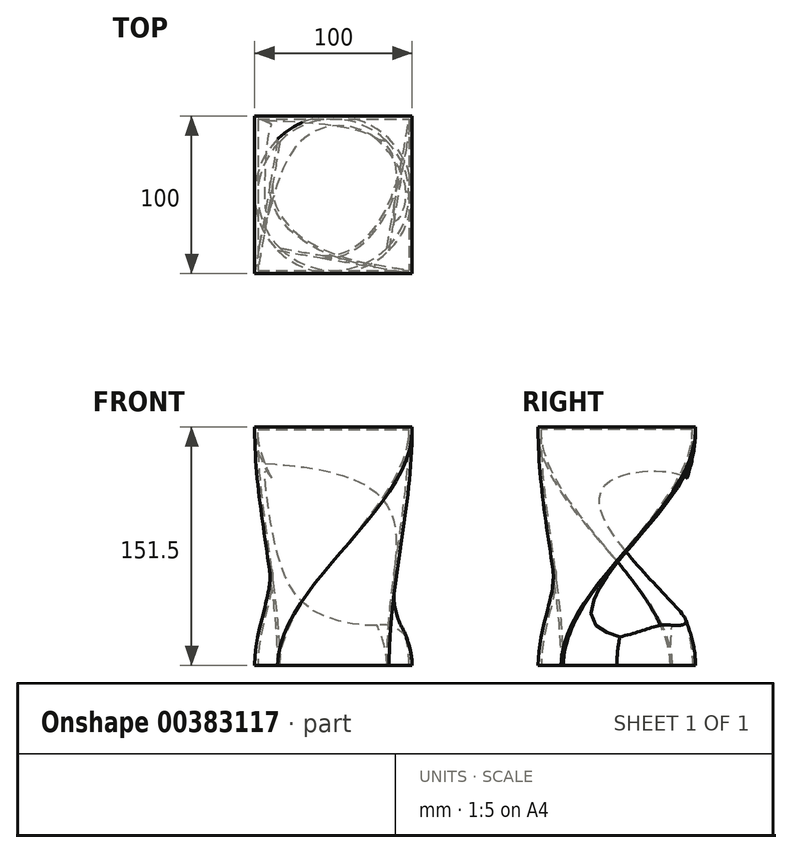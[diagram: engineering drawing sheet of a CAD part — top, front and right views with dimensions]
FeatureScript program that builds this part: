
annotation { "Feature Type Name" : "Feature", "Feature Type Description" : "" }
export const myFeature = defineFeature(function(context is Context, id is Id, definition is map)
    precondition{}
    {
        {
            var Q0;
            Q0=qCreatedBy(makeId("Top.planeOp"),FACE);
            var sketch = newSketch(context, id + "F0", { "sketchPlane" : qUnion([Q0])});
            skArc(sketch, "E0", {"start": v(-35.36, 35.36) * mm, "mid": v(-50, 0) * mm, "end": v(-35.36, -35.36) * mm});
            skArc(sketch, "E1", {"start": v(50, 0) * mm, "mid": v(19.13, 46.2) * mm, "end": v(-35.36, 35.36) * mm});
            skArc(sketch, "E2", {"start": v(-35.36, -35.36) * mm, "mid": v(35.36, -35.36) * mm, "end": v(35.36, 35.36) * mm});
            skArc(sketch, "E3", {"start": v(-35.36, -35.36) * mm, "mid": v(0, -50) * mm, "end": v(35.36, -35.36) * mm});
            skLineSegment(sketch, "E4", {"start": v(0, 57.4) * mm, "end": v(0, -65.17) * mm, "construction": true});
            skLineSegment(sketch, "E5", {"start": v(-56.88, 0) * mm, "end": v(63.58, 0) * mm, "construction": true});
            skLineSegment(sketch, "E6", {"start": v(0, 0) * mm, "end": v(35.36, 35.36) * mm, "construction": true});
            skLineSegment(sketch, "E7", {"start": v(0, 0) * mm, "end": v(-35.36, 35.36) * mm, "construction": true});
            skLineSegment(sketch, "E8", {"start": v(0, 0) * mm, "end": v(-35.36, -35.36) * mm, "construction": true});
            skLineSegment(sketch, "E9", {"start": v(0, 0) * mm, "end": v(35.36, -35.36) * mm, "construction": true});
            skSolve(sketch);
        }
        {
            var Q0;
            Q0=qCreatedBy(makeId("Top.planeOp"),FACE);
            cPlane(context, id + "F1", {"entities" : qUnion([Q0]), "cplaneType" : CPlaneType.OFFSET, "offset" : 150 * mm, "width" : 152.4 * mm, "height" : 152.4 * mm});
        }
        {
            var Q0;
            Q0=qCreatedBy(id+"F1.planeOp",FACE);
            var sketch = newSketch(context, id + "F2", { "sketchPlane" : qUnion([Q0])});
            skLineSegment(sketch, "E10.bottom", {"start": v(-50, 50) * mm, "end": v(50, 50) * mm});
            skLineSegment(sketch, "E10.top", {"start": v(-50, -50) * mm, "end": v(50, -50) * mm});
            skLineSegment(sketch, "E10.left", {"start": v(-50, 50) * mm, "end": v(-50, -50) * mm});
            skLineSegment(sketch, "E10.right", {"start": v(50, 50) * mm, "end": v(50, -50) * mm});
            skPoint(sketch, "E10.middle", {"position": v(0, 0) * mm});
            skSolve(sketch);
        }
        {
            var Q0;
            Q0=makeQuery(id+"F0.imprint","IMPRINT",FACE,{"disambiguationData":[TD([[makeQuery(id+"F0.imprint","IMPRINT",EDGE,{"derivedFrom":sQuery(id+"F0.wireOp",EDGE,"E0")}),1.0]])]});
            var Q1;
            Q1=makeQuery(id+"F2.imprint","IMPRINT",FACE,{"disambiguationData":[TD([[makeQuery(id+"F2.imprint","IMPRINT",EDGE,{"derivedFrom":sQuery(id+"F2.wireOp",EDGE,"E10.bottom")}),-1.0]])]});
            var Q2;
            Q2=sQuery(id+"F0.wireOp",VERTEX,"E3.end");
            var Q3;
            Q3=sQuery(id+"F2.wireOp",VERTEX,"E10.bottom.end");
            loft(context, id + "F3", {"startCondition" : LoftEndDerivativeType.NORMAL_TO_PROFILE, "startMagnitude" : 1, "endCondition" : LoftEndDerivativeType.NORMAL_TO_PROFILE, "endMagnitude" : 1, "sheetProfilesArray" : [{ "sheetProfileEntities" : qUnion([Q0]) }, { "sheetProfileEntities" : qUnion([Q1]) }], "matchConnections" : true, "connections" : [{ "connectionEntities" : qUnion([Q2, Q3]), "connectionEdgeQueries" : qUnion([]), "connectionEdgeParameters" : [] }]});
        }
        {
            var Q0;
            Q0=qCreatedBy(makeId("Top.planeOp"),FACE);
            var sketch = newSketch(context, id + "F4", { "sketchPlane" : qUnion([Q0])});
            skArc(sketch, "E11", {"start": v(-33.94, 33.94) * mm, "mid": v(-48, 0) * mm, "end": v(-33.94, -33.94) * mm});
            skArc(sketch, "E12", {"start": v(33.94, -33.94) * mm, "mid": v(33.94, 33.94) * mm, "end": v(-33.94, 33.94) * mm});
            skArc(sketch, "E13", {"start": v(33.94, -33.94) * mm, "mid": v(48, 0) * mm, "end": v(33.94, 33.94) * mm});
            skArc(sketch, "E14", {"start": v(-33.94, -33.94) * mm, "mid": v(0, -48) * mm, "end": v(33.94, -33.94) * mm});
            skSolve(sketch);
        }
        {
            var Q0;
            Q0=makeQuery(id+"F2.imprint","IMPRINT",FACE,{"disambiguationData":[TD([[makeQuery(id+"F2.imprint","IMPRINT",EDGE,{"derivedFrom":sQuery(id+"F2.wireOp",EDGE,"E10.bottom")}),-1.0]])]});
            var sketch = newSketch(context, id + "F5", { "sketchPlane" : qUnion([Q0])});
            skLineSegment(sketch, "E15.bottom", {"start": v(-48, 48) * mm, "end": v(48, 48) * mm});
            skLineSegment(sketch, "E15.top", {"start": v(-48, -48) * mm, "end": v(48, -48) * mm});
            skLineSegment(sketch, "E15.left", {"start": v(-48, 48) * mm, "end": v(-48, -48) * mm});
            skLineSegment(sketch, "E15.right", {"start": v(48, 48) * mm, "end": v(48, -48) * mm});
            skPoint(sketch, "E15.middle", {"position": v(0, 0) * mm});
            skSolve(sketch);
        }
        {
            var Q0;
            Q0=qSketchRegion(id+"F4",true);
            var Q1;
            Q1=qSketchRegion(id+"F5",true);
            var Q2;
            Q2=sQuery(id+"F4.wireOp",VERTEX,"E14.end");
            var Q3;
            Q3=sQuery(id+"F5.wireOp",VERTEX,"E15.right.start");
            loft(context, id + "F6", {"operationType" : NewBodyOperationType.REMOVE, "startCondition" : LoftEndDerivativeType.NORMAL_TO_PROFILE, "startMagnitude" : 1, "endCondition" : LoftEndDerivativeType.NORMAL_TO_PROFILE, "endMagnitude" : 1, "sheetProfilesArray" : [{ "sheetProfileEntities" : qUnion([Q0]) }, { "sheetProfileEntities" : qUnion([Q1]) }], "matchConnections" : true, "connections" : [{ "connectionEntities" : qUnion([Q2, Q3]), "connectionEdgeQueries" : qUnion([]), "connectionEdgeParameters" : [] }]});
        }
        {
            var Q0;
            Q0=makeQuery(id+"F5.imprint","IMPRINT",FACE,{"disambiguationData":[TD([[makeQuery(id+"F5.imprint","IMPRINT",EDGE,{"derivedFrom":sQuery(id+"F5.wireOp",EDGE,"E15.bottom")}),1.0]])]});
            var Q1;
            Q1=makeQuery(id+"F5.imprint","IMPRINT",FACE,{"disambiguationData":[TD([[makeQuery(id+"F5.imprint","IMPRINT",EDGE,{"derivedFrom":sQuery(id+"F5.wireOp",EDGE,"E15.bottom")}),-1.0]])]});
            extrude(context, id + "F7", {"entities" : qUnion([Q0, Q1]), "operationType" : NewBodyOperationType.ADD, "depth" : 1.5 * mm});
        }
    });
